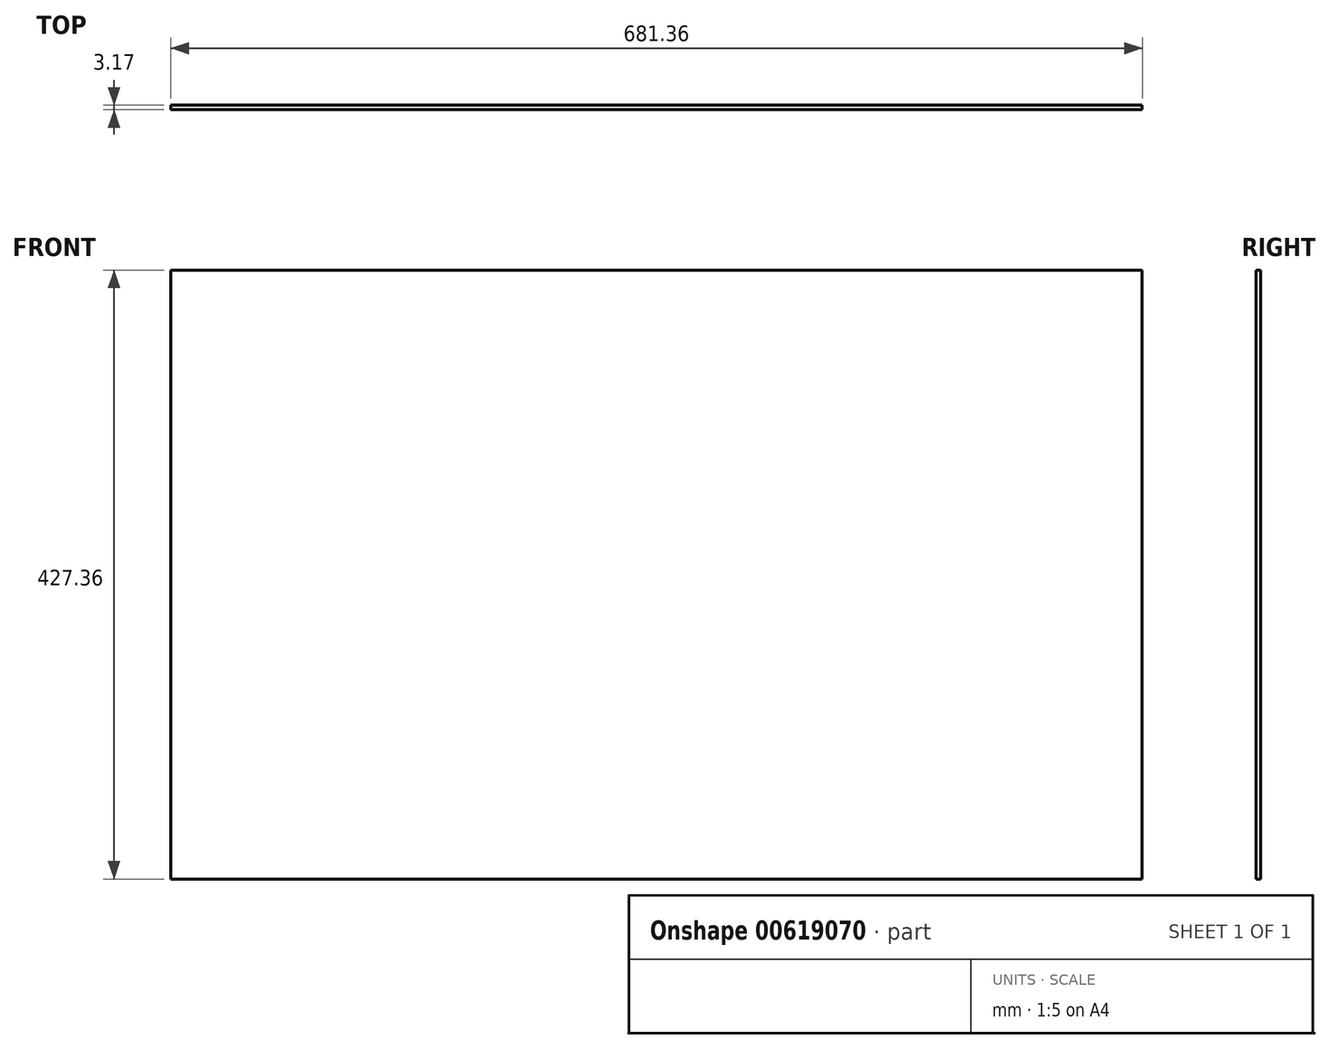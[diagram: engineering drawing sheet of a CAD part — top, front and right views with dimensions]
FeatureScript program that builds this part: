
annotation { "Feature Type Name" : "Feature", "Feature Type Description" : "" }
export const myFeature = defineFeature(function(context is Context, id is Id, definition is map)
    precondition{}
    {
        {
            var Q0;
            Q0=qCreatedBy(makeId("Front.planeOp"),FACE);
            var sketch = newSketch(context, id + "F0", { "sketchPlane" : qUnion([Q0])});
            skLineSegment(sketch, "E0.bottom", {"start": v(-375.88, 253.77) * mm, "end": v(305.48, 253.77) * mm});
            skLineSegment(sketch, "E0.top", {"start": v(-375.88, -173.59) * mm, "end": v(305.48, -173.59) * mm});
            skLineSegment(sketch, "E0.left", {"start": v(-375.88, 253.77) * mm, "end": v(-375.88, -173.59) * mm});
            skLineSegment(sketch, "E0.right", {"start": v(305.48, 253.77) * mm, "end": v(305.48, -173.59) * mm});
            skSolve(sketch);
        }
        {
            var Q0;
            Q0=qSketchRegion(id+"F0",true);
            extrude(context, id + "F1", {"entities" : qUnion([Q0]), "depth" : 3.17 * mm});
        }
    });
